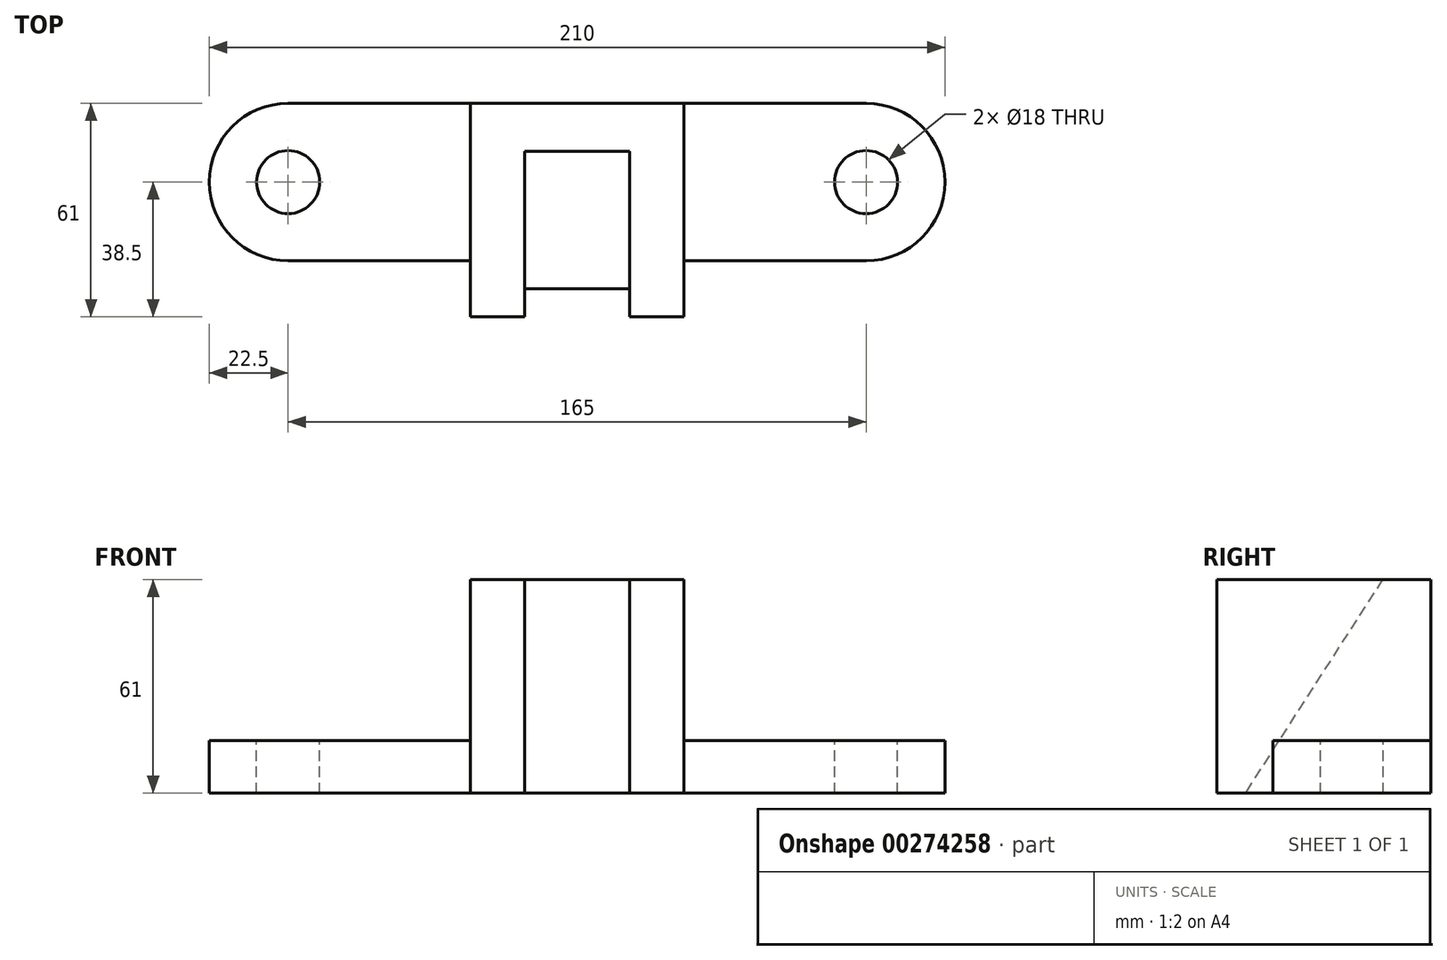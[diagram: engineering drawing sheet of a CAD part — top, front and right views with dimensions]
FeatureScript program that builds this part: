
annotation { "Feature Type Name" : "Feature", "Feature Type Description" : "" }
export const myFeature = defineFeature(function(context is Context, id is Id, definition is map)
    precondition{}
    {
        {
            var Q0;
            Q0=qCreatedBy(makeId("Front.planeOp"),FACE);
            var sketch = newSketch(context, id + "F0", { "sketchPlane" : qUnion([Q0])});
            skLineSegment(sketch, "E0.bottom", {"start": v(-30.5, 30.5) * mm, "end": v(30.5, 30.5) * mm});
            skLineSegment(sketch, "E0.top", {"start": v(-30.5, -30.5) * mm, "end": v(30.5, -30.5) * mm});
            skLineSegment(sketch, "E0.left", {"start": v(-30.5, 30.5) * mm, "end": v(-30.5, -30.5) * mm});
            skLineSegment(sketch, "E0.right", {"start": v(30.5, 30.5) * mm, "end": v(30.5, -30.5) * mm});
            skLineSegment(sketch, "E1.bottom", {"start": v(-30.5, -30.5) * mm, "end": v(-82.5, -30.5) * mm});
            skLineSegment(sketch, "E1.top", {"start": v(-30.5, -15.5) * mm, "end": v(-82.5, -15.5) * mm});
            skLineSegment(sketch, "E1.left", {"start": v(-30.5, -30.5) * mm, "end": v(-30.5, -15.5) * mm});
            skLineSegment(sketch, "E1.right", {"start": v(-82.5, -30.5) * mm, "end": v(-82.5, -15.5) * mm});
            skLineSegment(sketch, "E2.bottom", {"start": v(30.5, -30.5) * mm, "end": v(82.5, -30.5) * mm});
            skLineSegment(sketch, "E2.top", {"start": v(30.5, -15.5) * mm, "end": v(82.5, -15.5) * mm});
            skLineSegment(sketch, "E2.left", {"start": v(30.5, -30.5) * mm, "end": v(30.5, -15.5) * mm});
            skLineSegment(sketch, "E2.right", {"start": v(82.5, -30.5) * mm, "end": v(82.5, -15.5) * mm});
            skSolve(sketch);
        }
        {
            var Q0;
            Q0=makeQuery(id+"F0.imprint","IMPRINT",FACE,{"disambiguationData":[TD([[makeQuery(id+"F0.imprint","IMPRINT",EDGE,{"derivedFrom":sQuery(id+"F0.wireOp",EDGE,"E1.bottom")}),-1.0]])]});
            var Q1;
            Q1=makeQuery(id+"F0.imprint","IMPRINT",FACE,{"disambiguationData":[TD([[makeQuery(id+"F0.imprint","IMPRINT",EDGE,{"derivedFrom":sQuery(id+"F0.wireOp",EDGE,"E2.bottom")}),1.0]])]});
            extrude(context, id + "F1", {"entities" : qUnion([Q0, Q1]), "depth" : 45 * mm});
        }
        {
            var Q0;
            Q0=makeQuery(id+"F0.imprint","IMPRINT",FACE,{"disambiguationData":[TD([[makeQuery(id+"F0.imprint","IMPRINT",EDGE,{"derivedFrom":sQuery(id+"F0.wireOp",EDGE,"E0.bottom")}),-1.0]])]});
            extrude(context, id + "F2", {"entities" : qUnion([Q0]), "operationType" : NewBodyOperationType.ADD, "depth" : 61 * mm});
        }
        {
            var Q0;
            Q0=makeQuery(id+"F1.opExtrude","SWEPT_FACE",FACE,{"disambiguationData":[OSD([sQuery(id+"F0.wireOp",EDGE,"E1.top")])]});
            var sketch = newSketch(context, id + "F3", { "sketchPlane" : qUnion([Q0])});
            skCircle(sketch, "E3", {"center": v(-82.5, -22.5) * mm, "radius": 22.5 * mm});
            skLineSegment(sketch, "E4", {"start": v(-82.5, 0) * mm, "end": v(-82.5, -45) * mm});
            skArc(sketch, "E5", {"start": v(82.5, -45) * mm, "mid": v(105, -22.5) * mm, "end": v(82.5, 0) * mm});
            skLineSegment(sketch, "E6", {"start": v(82.5, 0) * mm, "end": v(82.5, -45) * mm});
            skSolve(sketch);
        }
        {
            var Q0;
            {var subQ0=sQuery(id+"F3.wireOp",EDGE,"E4");Q0=makeQuery(id+"F3.imprint","IMPRINT",FACE,{"disambiguationData":[TD([[makeQuery(id+"F3.imprint","IMPRINT",EDGE,{"derivedFrom":subQ0}),1.0]])]});}
            var Q1;
            Q1=makeQuery(id+"F3.imprint","IMPRINT",FACE,{"disambiguationData":[TD([[makeQuery(id+"F3.imprint","IMPRINT",EDGE,{"derivedFrom":sQuery(id+"F3.wireOp",EDGE,"E5")}),1.0]])]});
            extrude(context, id + "F4", {"entities" : qUnion([Q0, Q1]), "operationType" : NewBodyOperationType.ADD, "oppositeDirection" : true, "depth" : 15 * mm});
        }
        {
            var Q0;
            Q0=makeQuery(id+"F4.opExtrude","CAP_FACE",FACE,{"disambiguationData":[OSD([sQuery(id+"F3.wireOp",EDGE,"E3"),sQuery(id+"F3.wireOp",EDGE,"E4")])],"isStart":true});
            var sketch = newSketch(context, id + "F5", { "sketchPlane" : qUnion([Q0])});
            skCircle(sketch, "E7", {"center": v(-82.5, -22.5) * mm, "radius": 9 * mm});
            skSolve(sketch);
        }
        {
            var Q0;
            Q0=makeQuery(id+"F4.opExtrude","CAP_FACE",FACE,{"disambiguationData":[OSD([sQuery(id+"F3.wireOp",EDGE,"E5"),sQuery(id+"F3.wireOp",EDGE,"E6")])],"isStart":true});
            var sketch = newSketch(context, id + "F6", { "sketchPlane" : qUnion([Q0])});
            skCircle(sketch, "E8", {"center": v(82.5, -22.5) * mm, "radius": 9 * mm});
            skSolve(sketch);
        }
        {
            var Q0;
            Q0=makeQuery(id+"F6.imprint","IMPRINT",FACE,{"disambiguationData":[TD([[makeQuery(id+"F6.imprint","IMPRINT",EDGE,{"derivedFrom":sQuery(id+"F6.wireOp",EDGE,"E8")}),1.0]])]});
            var Q1;
            Q1=makeQuery(id+"F5.imprint","IMPRINT",FACE,{"disambiguationData":[TD([[makeQuery(id+"F5.imprint","IMPRINT",EDGE,{"derivedFrom":sQuery(id+"F5.wireOp",EDGE,"E7")}),1.0]])]});
            extrude(context, id + "F7", {"entities" : qUnion([Q0, Q1]), "operationType" : NewBodyOperationType.REMOVE, "oppositeDirection" : true, "depth" : 15 * mm});
        }
        {
            var Q0;
            Q0=makeQuery(id+"F2.opExtrude","SWEPT_FACE",FACE,{"disambiguationData":[OSD([sQuery(id+"F0.wireOp",EDGE,"E0.left"),sQuery(id+"F0.wireOp",EDGE,"E1.left")])]});
            cPlane(context, id + "F8", {"entities" : qUnion([Q0]), "cplaneType" : CPlaneType.OFFSET, "offset" : 15.5 * mm, "oppositeDirection" : true, "width" : 150 * mm, "height" : 150 * mm});
        }
        {
            var Q0;
            Q0=qCreatedBy(id+"F8.planeOp",FACE);
            var sketch = newSketch(context, id + "F9", { "sketchPlane" : qUnion([Q0])});
            skLineSegment(sketch, "E9", {"start": v(13.75, 30.5) * mm, "end": v(53, -30.5) * mm});
            skLineSegment(sketch, "E10", {"start": v(13.75, 30.5) * mm, "end": v(61, 30.5) * mm});
            skLineSegment(sketch, "E11", {"start": v(61, 30.5) * mm, "end": v(61, -30.5) * mm});
            skLineSegment(sketch, "E12", {"start": v(53, -30.5) * mm, "end": v(61, -30.5) * mm});
            skPoint(sketch, "E13.end.orphan", {"position": v(6, 30.5) * mm});
            skPoint(sketch, "E14.end.orphan", {"position": v(6, -30.5) * mm});
            skSolve(sketch);
        }
        {
            var Q0;
            Q0 = qSketchRegion(id + "F9", true);
            extrude(context, id + "F10", {"entities" : qUnion([Q0]), "operationType" : NewBodyOperationType.REMOVE, "oppositeDirection" : true, "depth" : 30 * mm});
        }
    });
